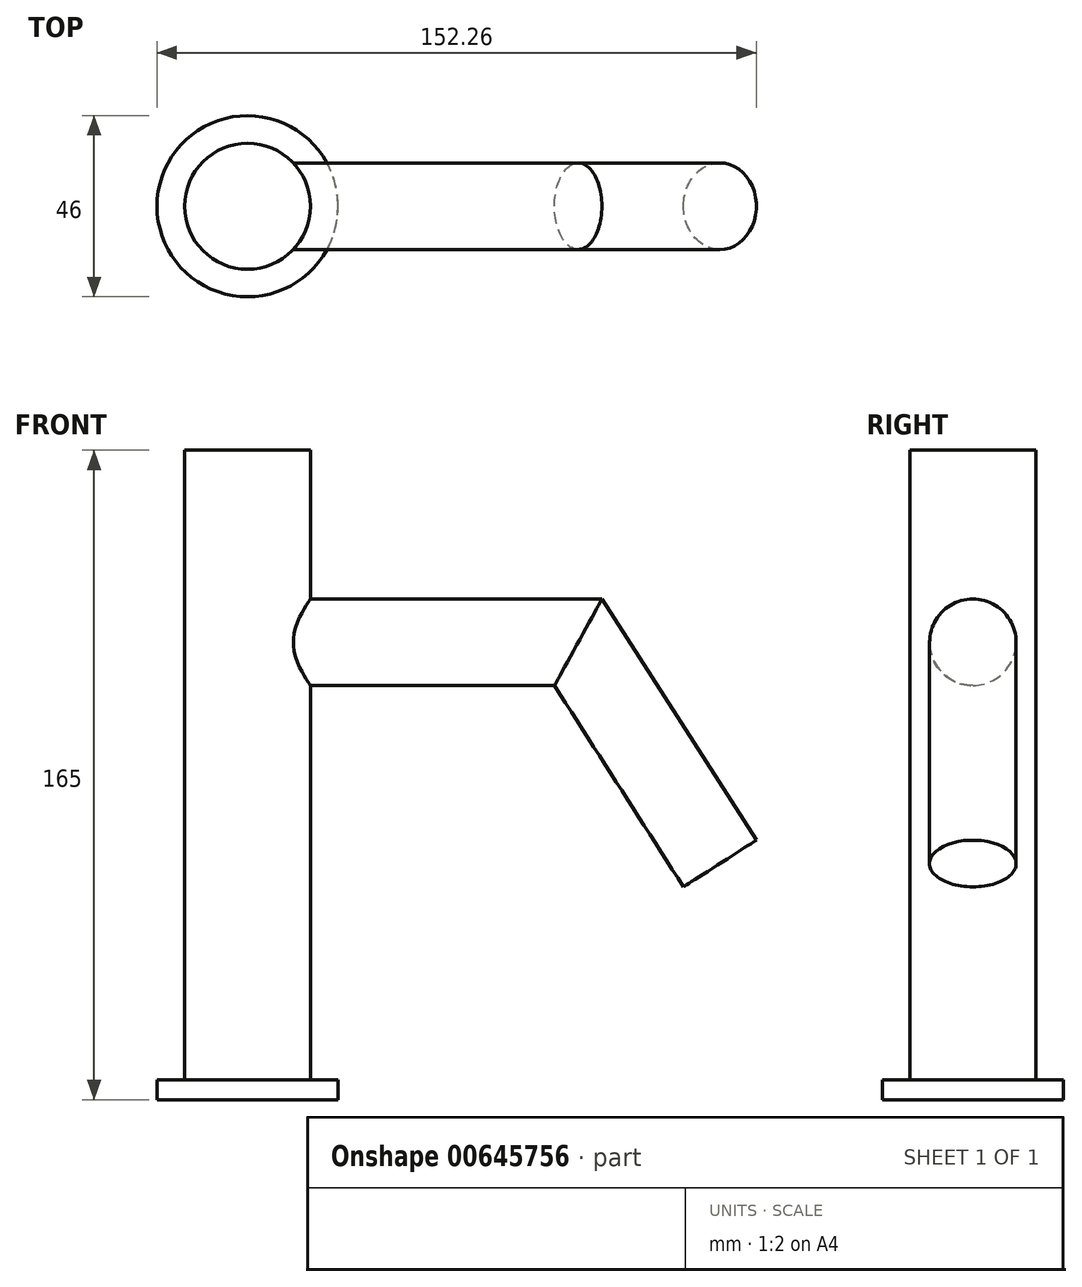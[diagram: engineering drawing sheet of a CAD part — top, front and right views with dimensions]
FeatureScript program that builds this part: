
annotation { "Feature Type Name" : "Feature", "Feature Type Description" : "" }
export const myFeature = defineFeature(function(context is Context, id is Id, definition is map)
    precondition{}
    {
        {
            var Q0;
            Q0=qCreatedBy(makeId("Top.planeOp"),FACE);
            var sketch = newSketch(context, id + "F0", { "sketchPlane" : qUnion([Q0])});
            skCircle(sketch, "E0", {"center": v(0, 0) * mm, "radius": 16 * mm});
            skSolve(sketch);
        }
        {
            var Q0;
            Q0=qSketchRegion(id+"F0",true);
            extrude(context, id + "F1", {"entities" : qUnion([Q0]), "depth" : 165 * mm, "offsetDistance" : 25 * mm});
        }
        {
            var Q0;
            Q0=qCreatedBy(makeId("Front.planeOp"),FACE);
            var sketch = newSketch(context, id + "F2", { "sketchPlane" : qUnion([Q0])});
            skLineSegment(sketch, "E1", {"start": v(0, 116.22) * mm, "end": v(186.98, 116.22) * mm, "construction": true});
            skLineSegment(sketch, "E2.bottom", {"start": v(0, 116.22) * mm, "end": v(84, 116.22) * mm});
            skLineSegment(sketch, "E2.top", {"start": v(0, 125.72) * mm, "end": v(89.2, 125.72) * mm});
            skLineSegment(sketch, "E2.left", {"start": v(0, 116.22) * mm, "end": v(0, 125.72) * mm});
            skLineSegment(sketch, "E3", {"start": v(89.2, 125.72) * mm, "end": v(128, 65.12) * mm});
            skLineSegment(sketch, "E4", {"start": v(120, 60) * mm, "end": v(128, 65.12) * mm});
            skLineSegment(sketch, "E5", {"start": v(120, 60) * mm, "end": v(112, 54.88) * mm, "construction": true});
            skLineSegment(sketch, "E6", {"start": v(120, 60) * mm, "end": v(84, 116.22) * mm});
            skLineSegment(sketch, "E7", {"start": v(120, 60) * mm, "end": v(191.8, 60) * mm, "construction": true});
            skLineSegment(sketch, "E8", {"start": v(-23, 131.1) * mm, "end": v(-23, -32.68) * mm, "construction": true});
            skSolve(sketch);
        }
        {
            var Q0;
            Q0=qCreatedBy(makeId("Front.planeOp"),FACE);
            var sketch = newSketch(context, id + "F3", { "sketchPlane" : qUnion([Q0])});
            skLineSegment(sketch, "E9.0", {"start": v(89.2, 125.72) * mm, "end": v(128, 65.12) * mm});
            skLineSegment(sketch, "E10.0", {"start": v(120, 60) * mm, "end": v(128, 65.12) * mm});
            skPoint(sketch, "E10.1", {"position": v(116, 57.44) * mm});
            skLineSegment(sketch, "E11", {"start": v(0, 0) * mm, "end": v(181.68, 0) * mm, "construction": true});
            skSolve(sketch);
        }
        {
            var Q0;
            Q0=qCreatedBy(makeId("Right.planeOp"),FACE);
            var sketch = newSketch(context, id + "F4", { "sketchPlane" : qUnion([Q0])});
            skCircle(sketch, "E12", {"center": v(0, 116.22) * mm, "radius": 11 * mm});
            skSolve(sketch);
        }
        {
            var Q0;
            Q0=qCreatedBy(makeId("Front.planeOp"),FACE);
            var sketch = newSketch(context, id + "F5", { "sketchPlane" : qUnion([Q0])});
            skLineSegment(sketch, "E13.0", {"start": v(0, 116.22) * mm, "end": v(84, 116.22) * mm});
            skLineSegment(sketch, "E14.0", {"start": v(120, 60) * mm, "end": v(84, 116.22) * mm});
            skSolve(sketch);
        }
        {
            var Q0;
            Q0=qSketchRegion(id+"F4",true);
            var Q1;
            Q1=qConstructionFilter(qBodyType(qCreatedBy(id+"F5",EDGE),BodyType.WIRE),ConstructionObject.NO);
            sweep(context, id + "F6", {"operationType" : NewBodyOperationType.ADD, "profiles" : qUnion([Q0]), "path" : qUnion([Q1])});
        }
        {
            var Q0;
            Q0=qCreatedBy(makeId("Top.planeOp"),FACE);
            var sketch = newSketch(context, id + "F7", { "sketchPlane" : qUnion([Q0])});
            skCircle(sketch, "E15", {"center": v(0, 0) * mm, "radius": 23 * mm});
            skSolve(sketch);
        }
        {
            var Q0;
            Q0=qSketchRegion(id+"F7",true);
            extrude(context, id + "F8", {"entities" : qUnion([Q0]), "operationType" : NewBodyOperationType.ADD, "depth" : 5 * mm, "offsetDistance" : 25 * mm});
        }
    });
